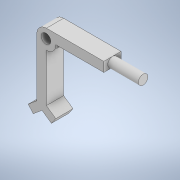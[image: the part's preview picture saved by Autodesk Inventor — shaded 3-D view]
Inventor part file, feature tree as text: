
AUTODESK INVENTOR PART (.ipt)
format: ipt  version: 2021 (Build 250183000, 183)  size: 121,856 bytes
history: native  units: mm
features: sketch x3, extrude x2, hole x1
ambient origin geometry x8: Origin, YZ Plane, XZ Plane, XY Plane, X Axis, Y Axis, Z Axis, Center Point
bodies: Solid1 (feature_tree)
feature tree (6):
  extrude  "Extrusion1"  Depth=80.0mm TaperAngle=0.0deg
  extrude  "Extrusion2"  Depth=150.0mm
  hole  "Hole1"  [1 undecoded]
  sketch  "Sketch1"  dims[d0=25.0mm d1=80.0mm d2=0.0mm]
  sketch  "Sketch2"  dims[d3=150.0mm d4=125.0mm]
  sketch  "Sketch3"  dims[d14=45.0mm d15=0.0mm d17=25.0mm d18=6.0mm d19=4.0mm d20=2.0mm d21=90.0deg d22=45.0mm d23=0.0mm]
note: 1 required parameter value undecoded (feature->parameter linkage not recoverable at this tier; creation-order binding heuristic only, values carry confidence <= 0.55)
